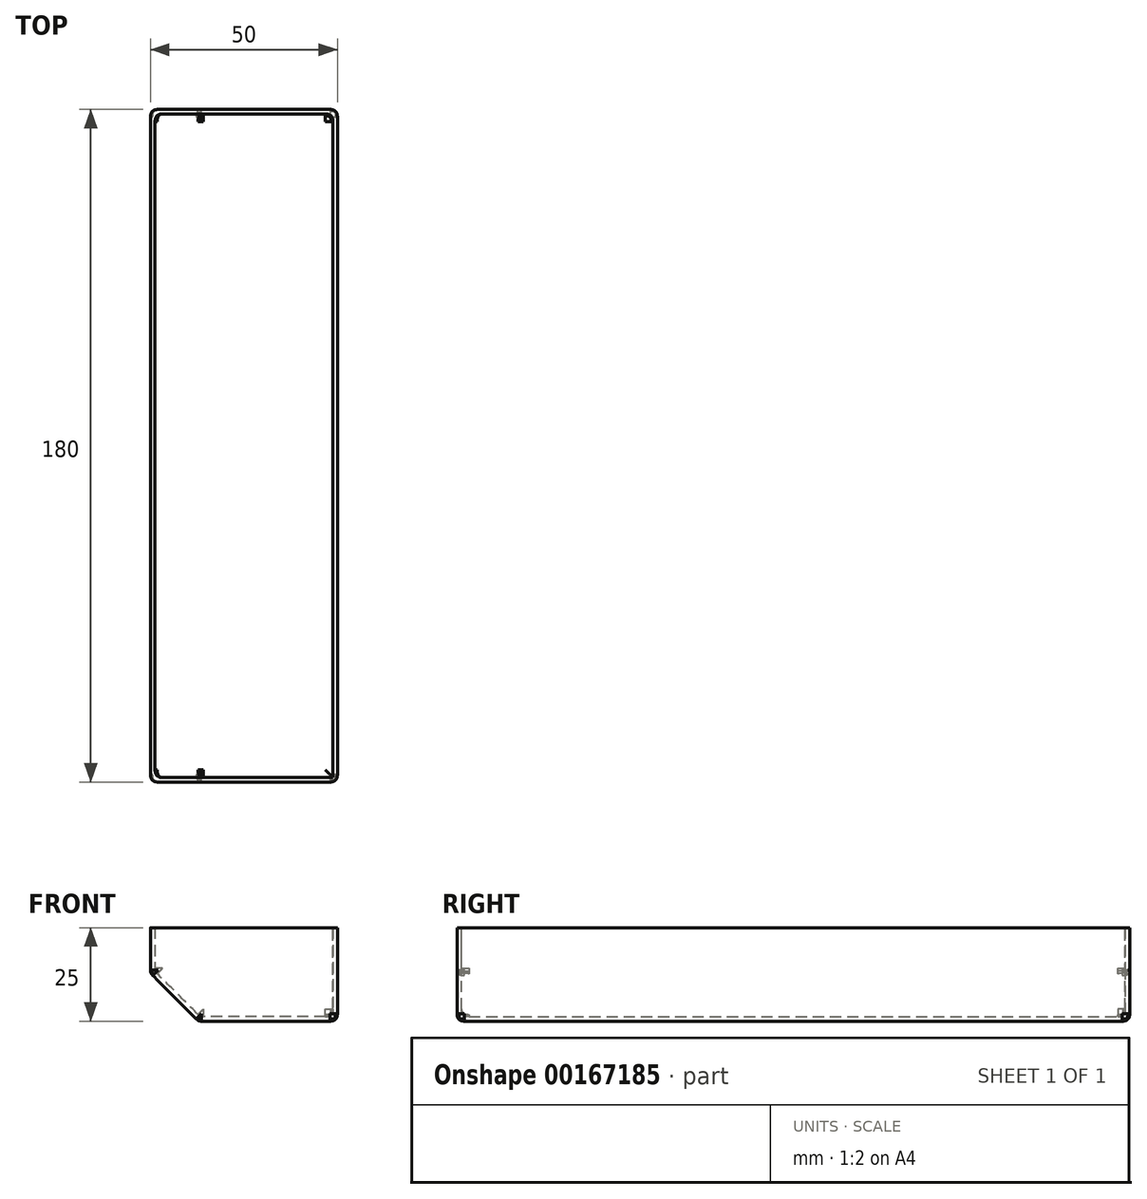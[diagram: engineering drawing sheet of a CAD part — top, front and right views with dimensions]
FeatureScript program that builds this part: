
annotation { "Feature Type Name" : "Feature", "Feature Type Description" : "" }
export const myFeature = defineFeature(function(context is Context, id is Id, definition is map)
    precondition{}
    {
        {
            var Q0;
            Q0=qCreatedBy(makeId("Front.planeOp"),FACE);
            var sketch = newSketch(context, id + "F0", { "sketchPlane" : qUnion([Q0])});
            skLineSegment(sketch, "E0", {"start": v(0, 0) * mm, "end": v(37.2, 0) * mm});
            skLineSegment(sketch, "E1", {"start": v(37.2, 0) * mm, "end": v(37.2, 25) * mm});
            skLineSegment(sketch, "E2", {"start": v(37.2, 25) * mm, "end": v(-12.8, 25) * mm});
            skLineSegment(sketch, "E3", {"start": v(-12.8, 25) * mm, "end": v(-12.8, 12.8) * mm});
            skLineSegment(sketch, "E4", {"start": v(-12.8, 12.8) * mm, "end": v(0, 0) * mm});
            skSolve(sketch);
        }
        {
            var Q0;
            Q0 = qSketchRegion(id + "F0", true);
            extrude(context, id + "F1", {"entities" : qUnion([Q0]), "depth" : 180 * mm});
        }
        {
            var Q0;
            Q0=makeQuery(id+"F1.opExtrude","SWEPT_FACE",FACE,{"disambiguationData":[OSD([sQuery(id+"F0.wireOp",EDGE,"E2")])]});
            var Q1;
            Q1=makeQuery(id+"F1.opExtrude","SWEPT_BODY",BODY,{"disambiguationData":[OSD([sQuery(id+"F0.wireOp",EDGE,"E0"),sQuery(id+"F0.wireOp",EDGE,"E1"),sQuery(id+"F0.wireOp",EDGE,"E2"),sQuery(id+"F0.wireOp",EDGE,"E3"),sQuery(id+"F0.wireOp",EDGE,"E4")])]});
            shell(context, id + "F2", {"entities" : qUnion([Q0]), "parts" : qUnion([Q1]), "thickness" : 1.2 * mm});
        }
        {
            var Q0;
            {var subQ0=sQuery(id+"F0.wireOp",EDGE,"E0");Q0=makeQuery(id+"F2.opShell","OFFSET_EDGE",EDGE,{"disambiguationData":[OSD([subQ0]),TDD([makeQuery(id+"F1.opExtrude","CAP_EDGE",EDGE,{"disambiguationData":[OSD([subQ0])],"isStart":true})])]});}
            var Q1;
            Q1=makeQuery(id+"F2.opShell","OFFSET_EDGE",EDGE,{"disambiguationData":[OSD([sQuery(id+"F0.wireOp",EDGE,"E0"),sQuery(id+"F0.wireOp",EDGE,"E4")])]});
            var Q2;
            Q2=makeQuery(id+"F2.opShell","OFFSET_EDGE",EDGE,{"disambiguationData":[OSD([sQuery(id+"F0.wireOp",EDGE,"E0"),sQuery(id+"F0.wireOp",EDGE,"E1")])]});
            var Q3;
            {var subQ0=sQuery(id+"F0.wireOp",EDGE,"E0");Q3=makeQuery(id+"F2.opShell","OFFSET_EDGE",EDGE,{"disambiguationData":[OSD([subQ0]),TDD([makeQuery(id+"F1.opExtrude","CAP_EDGE",EDGE,{"disambiguationData":[OSD([subQ0])],"isStart":false})])]});}
            var Q4;
            {var subQ0=sQuery(id+"F0.wireOp",EDGE,"E4");Q4=makeQuery(id+"F2.opShell","OFFSET_EDGE",EDGE,{"disambiguationData":[OSD([subQ0]),TDD([makeQuery(id+"F1.opExtrude","CAP_EDGE",EDGE,{"disambiguationData":[OSD([subQ0])],"isStart":false})])]});}
            var Q5;
            {var subQ0=sQuery(id+"F0.wireOp",EDGE,"E4");Q5=makeQuery(id+"F2.opShell","OFFSET_EDGE",EDGE,{"disambiguationData":[OSD([subQ0]),TDD([makeQuery(id+"F1.opExtrude","CAP_EDGE",EDGE,{"disambiguationData":[OSD([subQ0])],"isStart":true})])]});}
            var Q6;
            Q6=makeQuery(id+"F2.opShell","OFFSET_EDGE",EDGE,{"disambiguationData":[OSD([sQuery(id+"F0.wireOp",EDGE,"E3"),sQuery(id+"F0.wireOp",EDGE,"E4")])]});
            var Q7;
            {var subQ0=sQuery(id+"F0.wireOp",EDGE,"E1");Q7=makeQuery(id+"F2.opShell","OFFSET_EDGE",EDGE,{"disambiguationData":[OSD([subQ0]),TDD([makeQuery(id+"F1.opExtrude","CAP_EDGE",EDGE,{"disambiguationData":[OSD([subQ0])],"isStart":true})])]});}
            var Q8;
            {var subQ0=sQuery(id+"F0.wireOp",EDGE,"E3");Q8=makeQuery(id+"F2.opShell","OFFSET_EDGE",EDGE,{"disambiguationData":[OSD([subQ0]),TDD([makeQuery(id+"F1.opExtrude","CAP_EDGE",EDGE,{"disambiguationData":[OSD([subQ0])],"isStart":false})])]});}
            var Q9;
            {var subQ0=sQuery(id+"F0.wireOp",EDGE,"E3");Q9=makeQuery(id+"F2.opShell","OFFSET_EDGE",EDGE,{"disambiguationData":[OSD([subQ0]),TDD([makeQuery(id+"F1.opExtrude","CAP_EDGE",EDGE,{"disambiguationData":[OSD([subQ0])],"isStart":true})])]});}
            var Q10;
            Q10=makeQuery(id+"F1.opExtrude","SWEPT_EDGE",EDGE,{"disambiguationData":[OSD([sQuery(id+"F0.wireOp",EDGE,"E0"),sQuery(id+"F0.wireOp",EDGE,"E4")])]});
            var Q11;
            Q11=makeQuery(id+"F1.opExtrude","SWEPT_EDGE",EDGE,{"disambiguationData":[OSD([sQuery(id+"F0.wireOp",EDGE,"E3"),sQuery(id+"F0.wireOp",EDGE,"E4")])]});
            var Q12;
            Q12=makeQuery(id+"F1.opExtrude","SWEPT_EDGE",EDGE,{"disambiguationData":[OSD([sQuery(id+"F0.wireOp",EDGE,"E0"),sQuery(id+"F0.wireOp",EDGE,"E1")])]});
            var Q13;
            Q13=makeQuery(id+"F1.opExtrude","CAP_EDGE",EDGE,{"disambiguationData":[OSD([sQuery(id+"F0.wireOp",EDGE,"E3")])],"isStart":false});
            var Q14;
            Q14=makeQuery(id+"F1.opExtrude","CAP_EDGE",EDGE,{"disambiguationData":[OSD([sQuery(id+"F0.wireOp",EDGE,"E4")])],"isStart":false});
            var Q15;
            Q15=makeQuery(id+"F1.opExtrude","CAP_EDGE",EDGE,{"disambiguationData":[OSD([sQuery(id+"F0.wireOp",EDGE,"E0")])],"isStart":false});
            var Q16;
            Q16=makeQuery(id+"F1.opExtrude","CAP_EDGE",EDGE,{"disambiguationData":[OSD([sQuery(id+"F0.wireOp",EDGE,"E1")])],"isStart":false});
            var Q17;
            Q17=makeQuery(id+"F1.opExtrude","CAP_EDGE",EDGE,{"disambiguationData":[OSD([sQuery(id+"F0.wireOp",EDGE,"E1")])],"isStart":true});
            var Q18;
            Q18=makeQuery(id+"F1.opExtrude","CAP_EDGE",EDGE,{"disambiguationData":[OSD([sQuery(id+"F0.wireOp",EDGE,"E0")])],"isStart":true});
            var Q19;
            Q19=makeQuery(id+"F1.opExtrude","CAP_EDGE",EDGE,{"disambiguationData":[OSD([sQuery(id+"F0.wireOp",EDGE,"E4")])],"isStart":true});
            var Q20;
            Q20=makeQuery(id+"F1.opExtrude","CAP_EDGE",EDGE,{"disambiguationData":[OSD([sQuery(id+"F0.wireOp",EDGE,"E3")])],"isStart":true});
            fillet(context, id + "F3", {"entities" : qUnion([Q0, Q1, Q2, Q3, Q4, Q5, Q6, Q7, Q8, Q9, Q10, Q11, Q12, Q13, Q14, Q15, Q16, Q17, Q18, Q19, Q20]), "radius" : 2 * mm, "rho" : 0.5, "crossSection" : FilletCrossSection.CONIC, "allowEdgeOverflow" : false});
        }
    });
